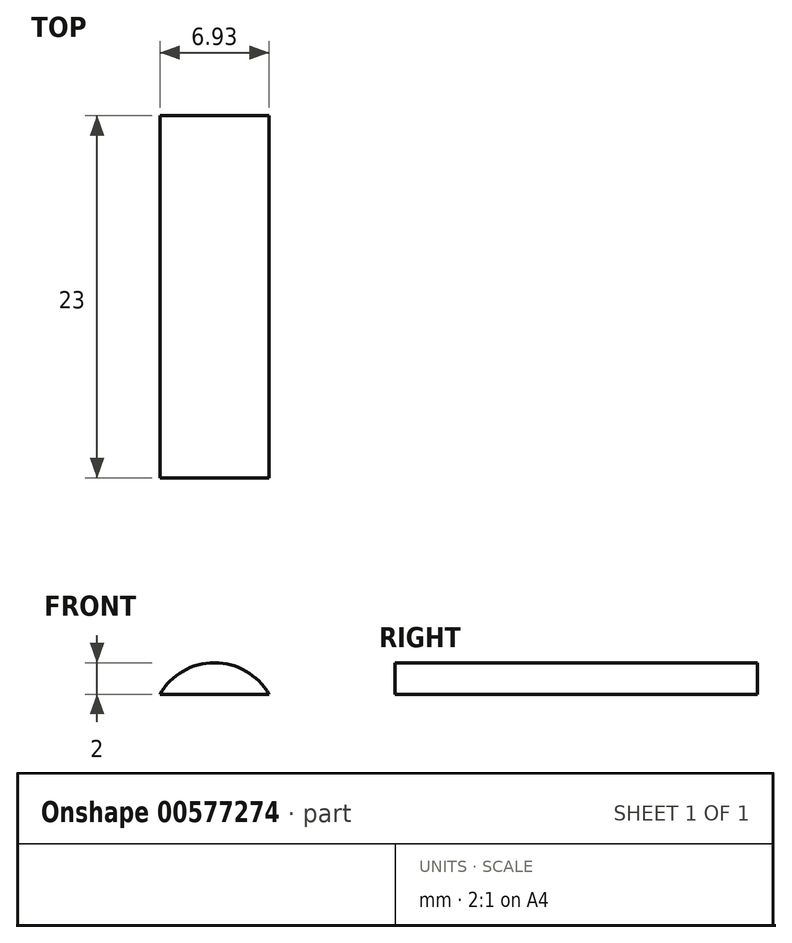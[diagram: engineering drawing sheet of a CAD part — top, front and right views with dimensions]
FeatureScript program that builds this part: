
annotation { "Feature Type Name" : "Feature", "Feature Type Description" : "" }
export const myFeature = defineFeature(function(context is Context, id is Id, definition is map)
    precondition{}
    {
        {
            var Q0;
            Q0=qCreatedBy(makeId("Front.planeOp"),FACE);
            var sketch = newSketch(context, id + "F0", { "sketchPlane" : qUnion([Q0])});
            skArc(sketch, "E0", {"start": v(6.56, 14) * mm, "mid": v(3.1, 16) * mm, "end": v(-0.37, 14) * mm});
            skLineSegment(sketch, "E1", {"start": v(-0.37, 14) * mm, "end": v(6.56, 14) * mm});
            skSolve(sketch);
        }
        {
            var Q0;
            Q0 = qSketchRegion(id + "F0", true);
            extrude(context, id + "F1", {"entities" : qUnion([Q0]), "depth" : 23 * mm, "offsetDistance" : 25 * mm});
        }
    });
